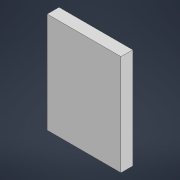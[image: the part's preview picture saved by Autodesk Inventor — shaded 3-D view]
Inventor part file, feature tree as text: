
AUTODESK INVENTOR PART (.ipt)
format: ipt  version: 2022 (Build 260153070, 153G)  size: 88,576 bytes
history: native  units: mm
features: sketch x1, extrude x1
ambient origin geometry x8: Origin, YZ Plane, XZ Plane, XY Plane, X Axis, Y Axis, Z Axis, Center Point
bodies: Body1 (feature_tree)
feature tree (2):
  sketch  "Эскиз1"
  extrude  "Выдавливание2"  Depth=250.0mm
